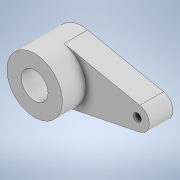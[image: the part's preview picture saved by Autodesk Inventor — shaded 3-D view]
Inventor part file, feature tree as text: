
AUTODESK INVENTOR PART (.ipt)
format: ipt  version: 2020 (Build 240168000, 168)  size: 122,880 bytes
history: native  units: mm
features: extrude x2, sketch x2, projected_geometry x1
ambient origin geometry x8: Origin, YZ Plane, XZ Plane, XY Plane, X Axis, Y Axis, Z Axis, Center Point
bodies: Solid1 (feature_tree)
feature tree (5):
  extrude  "Extrusion1"  Depth=7.0mm
  extrude  "Extrusion2"  Depth=3.0mm
  sketch  "Sketch1"  dims[d0=3.4mm d1=7.0mm]
  sketch  "Sketch2"  dims[d2=3.0mm d3=1.0mm d4=10.0mm d5=3.0mm d6=0.0mm d7=3.0mm d8=0.0mm]
  projected_geometry  "Projected Loop1"
